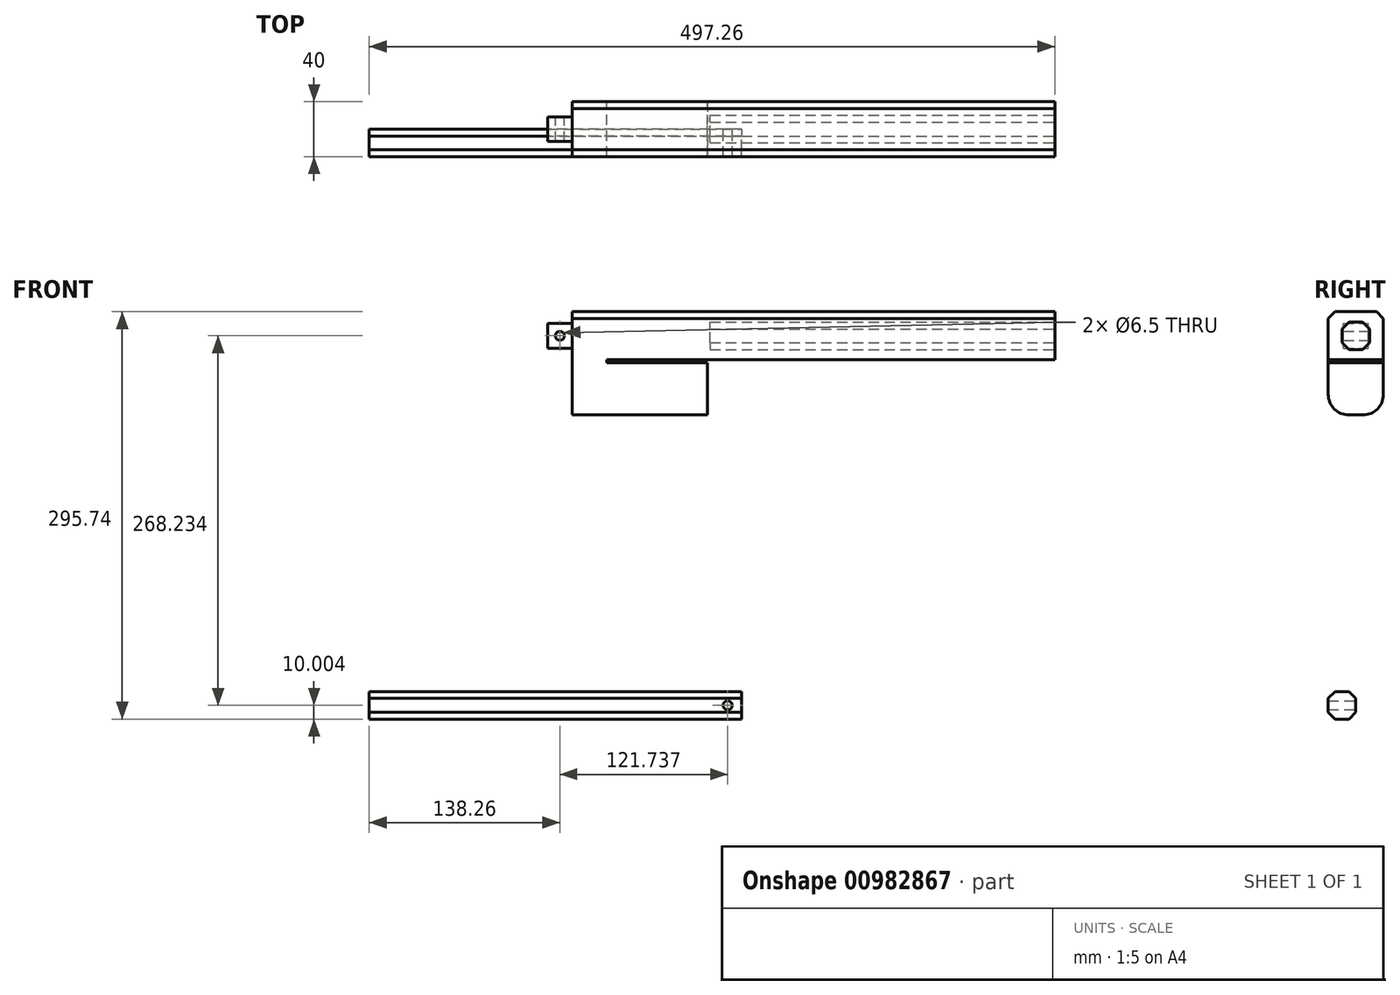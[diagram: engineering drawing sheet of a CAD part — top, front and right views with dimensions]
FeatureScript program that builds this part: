
annotation { "Feature Type Name" : "Feature", "Feature Type Description" : "" }
export const myFeature = defineFeature(function(context is Context, id is Id, definition is map)
    precondition{}
    {
        {
            var Q0;
            Q0=qCreatedBy(makeId("Front.planeOp"),FACE);
            var sketch = newSketch(context, id + "F0", { "sketchPlane" : qUnion([Q0])});
            skLineSegment(sketch, "E0.bottom", {"start": v(-368, -16.06) * mm, "end": v(-350, -16.06) * mm});
            skLineSegment(sketch, "E0.top", {"start": v(-368, 1.94) * mm, "end": v(-350, 1.94) * mm});
            skLineSegment(sketch, "E0.left", {"start": v(-368, -16.06) * mm, "end": v(-368, 1.94) * mm});
            skLineSegment(sketch, "E0.right", {"start": v(-350, -16.06) * mm, "end": v(-350, 1.94) * mm});
            skLineSegment(sketch, "E1.bottom", {"start": v(-350, 10.44) * mm, "end": v(-325, 10.44) * mm});
            skLineSegment(sketch, "E1.top", {"start": v(-350, -64.56) * mm, "end": v(-325, -64.56) * mm});
            skLineSegment(sketch, "E1.left", {"start": v(-350, 10.44) * mm, "end": v(-350, -64.56) * mm});
            skLineSegment(sketch, "E1.right", {"start": v(-325, 10.44) * mm, "end": v(-325, -64.56) * mm});
            skLineSegment(sketch, "E2.bottom", {"start": v(-325, -64.56) * mm, "end": v(-252, -64.56) * mm});
            skLineSegment(sketch, "E2.top", {"start": v(-325, -26.56) * mm, "end": v(-252, -26.56) * mm});
            skLineSegment(sketch, "E2.left", {"start": v(-325, -64.56) * mm, "end": v(-325, -26.56) * mm});
            skLineSegment(sketch, "E2.right", {"start": v(-252, -64.56) * mm, "end": v(-252, -26.56) * mm});
            skLineSegment(sketch, "E3.bottom", {"start": v(-325, 10.44) * mm, "end": v(0, 10.44) * mm});
            skLineSegment(sketch, "E3.top", {"start": v(-325, -24.56) * mm, "end": v(0, -24.56) * mm});
            skLineSegment(sketch, "E3.left", {"start": v(-325, 10.44) * mm, "end": v(-325, -24.56) * mm});
            skLineSegment(sketch, "E3.right", {"start": v(0, 10.44) * mm, "end": v(0, -24.56) * mm});
            skCircle(sketch, "E4", {"center": v(-359, -7.06) * mm, "radius": 3.25 * mm});
            skLineSegment(sketch, "E5.bottom", {"start": v(-497.26, -285.3) * mm, "end": v(-227.26, -285.3) * mm});
            skLineSegment(sketch, "E5.top", {"start": v(-497.26, -265.3) * mm, "end": v(-227.26, -265.3) * mm});
            skLineSegment(sketch, "E5.left", {"start": v(-497.26, -285.3) * mm, "end": v(-497.26, -265.3) * mm});
            skLineSegment(sketch, "E5.right", {"start": v(-227.26, -285.3) * mm, "end": v(-227.26, -265.3) * mm});
            skCircle(sketch, "E6", {"center": v(-237.26, -275.3) * mm, "radius": 3.25 * mm});
            skSolve(sketch);
        }
        {
            var Q0;
            {var subQ1=sQuery(id+"F0.wireOp",EDGE,"E0.bottom");Q0=makeQuery(id+"F0.imprint","IMPRINT",FACE,{"disambiguationData":[TD([[makeQuery(id+"F0.imprint","IMPRINT",EDGE,{"derivedFrom":subQ1}),1.0]])]});}
            extrude(context, id + "F1", {"entities" : qUnion([Q0]), "depth" : 9 * mm, "offsetDistance" : 25 * mm, "hasSecondDirection" : true, "secondDirectionOppositeDirection" : true, "secondDirectionDepth" : 9 * mm});
        }
        {
            var Q0;
            {var subQ3=sQuery(id+"F0.wireOp",EDGE,"E1.bottom");Q0=makeQuery(id+"F0.imprint","IMPRINT",FACE,{"disambiguationData":[TD([[makeQuery(id+"F0.imprint","IMPRINT",EDGE,{"derivedFrom":subQ3}),-1.0]])]});}
            var Q1;
            Q1=makeQuery(id+"F0.imprint","IMPRINT",FACE,{"disambiguationData":[TD([[makeQuery(id+"F0.imprint","IMPRINT",EDGE,{"derivedFrom":sQuery(id+"F0.wireOp",EDGE,"E3.bottom")}),-1.0]])]});
            var Q2;
            Q2=makeQuery(id+"F0.imprint","IMPRINT",FACE,{"disambiguationData":[TD([[makeQuery(id+"F0.imprint","IMPRINT",EDGE,{"derivedFrom":sQuery(id+"F0.wireOp",EDGE,"E2.bottom")}),1.0]])]});
            extrude(context, id + "F2", {"entities" : qUnion([Q0, Q1, Q2]), "operationType" : NewBodyOperationType.ADD, "depth" : 20 * mm, "offsetDistance" : 25 * mm, "hasSecondDirection" : true, "secondDirectionOppositeDirection" : true, "secondDirectionDepth" : 20 * mm});
        }
        {
            var Q0;
            Q0=makeQuery(id+"F2.opExtrude","CAP_EDGE",EDGE,{"disambiguationData":[OSD([sQuery(id+"F0.wireOp",EDGE,"E1.bottom"),sQuery(id+"F0.wireOp",EDGE,"E3.bottom")])],"isStart":true});
            var Q1;
            Q1=makeQuery(id+"F2.opExtrude","CAP_EDGE",EDGE,{"disambiguationData":[OSD([sQuery(id+"F0.wireOp",EDGE,"E1.bottom"),sQuery(id+"F0.wireOp",EDGE,"E3.bottom")])],"isStart":false});
            chamfer(context, id + "F3", {"entities" : qUnion([Q0, Q1]), "width" : 5 * mm, "tangentPropagation" : true});
        }
        {
            var Q0;
            Q0=makeQuery(id+"F2.opExtrude","CAP_EDGE",EDGE,{"disambiguationData":[OSD([sQuery(id+"F0.wireOp",EDGE,"E1.top"),sQuery(id+"F0.wireOp",EDGE,"E2.bottom")])],"isStart":true});
            var Q1;
            Q1=makeQuery(id+"F2.opExtrude","CAP_EDGE",EDGE,{"disambiguationData":[OSD([sQuery(id+"F0.wireOp",EDGE,"E1.top"),sQuery(id+"F0.wireOp",EDGE,"E2.bottom")])],"isStart":false});
            fillet(context, id + "F4", {"entities" : qUnion([Q0, Q1]), "radius" : 15 * mm, "tangentPropagation" : true, "allowEdgeOverflow" : false});
        }
        {
            var Q0;
            Q0=makeQuery(id+"F2.opExtrude","SWEPT_FACE",FACE,{"disambiguationData":[OSD([sQuery(id+"F0.wireOp",EDGE,"E3.right")])]});
            var sketch = newSketch(context, id + "F5", { "sketchPlane" : qUnion([Q0])});
            skLineSegment(sketch, "E7.bottom", {"start": v(-10, -17.06) * mm, "end": v(10, -17.06) * mm});
            skLineSegment(sketch, "E7.top", {"start": v(-10, 2.94) * mm, "end": v(10, 2.94) * mm});
            skLineSegment(sketch, "E7.left", {"start": v(-10, -17.06) * mm, "end": v(-10, 2.94) * mm});
            skLineSegment(sketch, "E7.right", {"start": v(10, -17.06) * mm, "end": v(10, 2.94) * mm});
            skLineSegment(sketch, "E8", {"start": v(-10, -2.06) * mm, "end": v(-5, -2.06) * mm});
            skLineSegment(sketch, "E9", {"start": v(-5, -2.06) * mm, "end": v(-5, 2.94) * mm});
            skLineSegment(sketch, "E10", {"start": v(-5, 2.94) * mm, "end": v(-10, -2.06) * mm});
            skLineSegment(sketch, "E11", {"start": v(5, 2.94) * mm, "end": v(5, -2.06) * mm});
            skLineSegment(sketch, "E12", {"start": v(5, -2.06) * mm, "end": v(10, -2.06) * mm});
            skLineSegment(sketch, "E13", {"start": v(10, -2.06) * mm, "end": v(5, 2.94) * mm});
            skLineSegment(sketch, "E14", {"start": v(10, -12.06) * mm, "end": v(5, -12.06) * mm});
            skLineSegment(sketch, "E15", {"start": v(5, -12.06) * mm, "end": v(5, -17.06) * mm});
            skLineSegment(sketch, "E16", {"start": v(5, -17.06) * mm, "end": v(10, -12.06) * mm});
            skLineSegment(sketch, "E17", {"start": v(-5, -17.06) * mm, "end": v(-5, -12.06) * mm});
            skLineSegment(sketch, "E18", {"start": v(-5, -12.06) * mm, "end": v(-10, -12.06) * mm});
            skLineSegment(sketch, "E19", {"start": v(-10, -12.06) * mm, "end": v(-5, -17.06) * mm});
            skSolve(sketch);
        }
        {
            var Q0;
            Q0=makeQuery(id+"F5.imprint","IMPRINT",FACE,{"disambiguationData":[TD([[makeQuery(id+"F5.imprint","IMPRINT",EDGE,{"derivedFrom":sQuery(id+"F5.wireOp",EDGE,"E17")}),1.0]])]});
            var Q1;
            {var subQ3=sQuery(id+"F5.wireOp",EDGE,"E8");Q1=makeQuery(id+"F5.imprint","IMPRINT",FACE,{"disambiguationData":[TD([[makeQuery(id+"F5.imprint","IMPRINT",EDGE,{"derivedFrom":subQ3}),-1.0]])]});}
            var Q2;
            Q2=makeQuery(id+"F5.imprint","IMPRINT",FACE,{"disambiguationData":[TD([[makeQuery(id+"F5.imprint","IMPRINT",EDGE,{"derivedFrom":sQuery(id+"F5.wireOp",EDGE,"E14")}),1.0]])]});
            var Q3;
            Q3=makeQuery(id+"F5.imprint","IMPRINT",FACE,{"disambiguationData":[TD([[makeQuery(id+"F5.imprint","IMPRINT",EDGE,{"derivedFrom":sQuery(id+"F5.wireOp",EDGE,"E11")}),1.0]])]});
            var Q4;
            Q4=makeQuery(id+"F5.imprint","IMPRINT",FACE,{"disambiguationData":[TD([[makeQuery(id+"F5.imprint","IMPRINT",EDGE,{"derivedFrom":sQuery(id+"F5.wireOp",EDGE,"E8")}),1.0]])]});
            extrude(context, id + "F6", {"entities" : qUnion([Q0, Q1, Q2, Q3, Q4]), "operationType" : NewBodyOperationType.REMOVE, "oppositeDirection" : true, "depth" : 250 * mm, "offsetDistance" : 25 * mm});
        }
        {
            var Q0;
            Q0=makeQuery(id+"F0.imprint","IMPRINT",FACE,{"disambiguationData":[TD([[makeQuery(id+"F0.imprint","IMPRINT",EDGE,{"derivedFrom":sQuery(id+"F0.wireOp",EDGE,"E5.bottom")}),1.0]])]});
            extrude(context, id + "F7", {"entities" : qUnion([Q0]), "depth" : 20 * mm, "offsetDistance" : 25 * mm});
        }
        {
            var Q0;
            Q0=makeQuery(id+"F7.opExtrude","CAP_EDGE",EDGE,{"disambiguationData":[OSD([sQuery(id+"F0.wireOp",EDGE,"E5.bottom")])],"isStart":true});
            var Q1;
            Q1=makeQuery(id+"F7.opExtrude","CAP_EDGE",EDGE,{"disambiguationData":[OSD([sQuery(id+"F0.wireOp",EDGE,"E5.top")])],"isStart":true});
            var Q2;
            Q2=makeQuery(id+"F7.opExtrude","CAP_EDGE",EDGE,{"disambiguationData":[OSD([sQuery(id+"F0.wireOp",EDGE,"E5.top")])],"isStart":false});
            var Q3;
            Q3=makeQuery(id+"F7.opExtrude","CAP_EDGE",EDGE,{"disambiguationData":[OSD([sQuery(id+"F0.wireOp",EDGE,"E5.bottom")])],"isStart":false});
            chamfer(context, id + "F8", {"entities" : qUnion([Q0, Q1, Q2, Q3]), "width" : 5 * mm, "tangentPropagation" : true});
        }
    });
